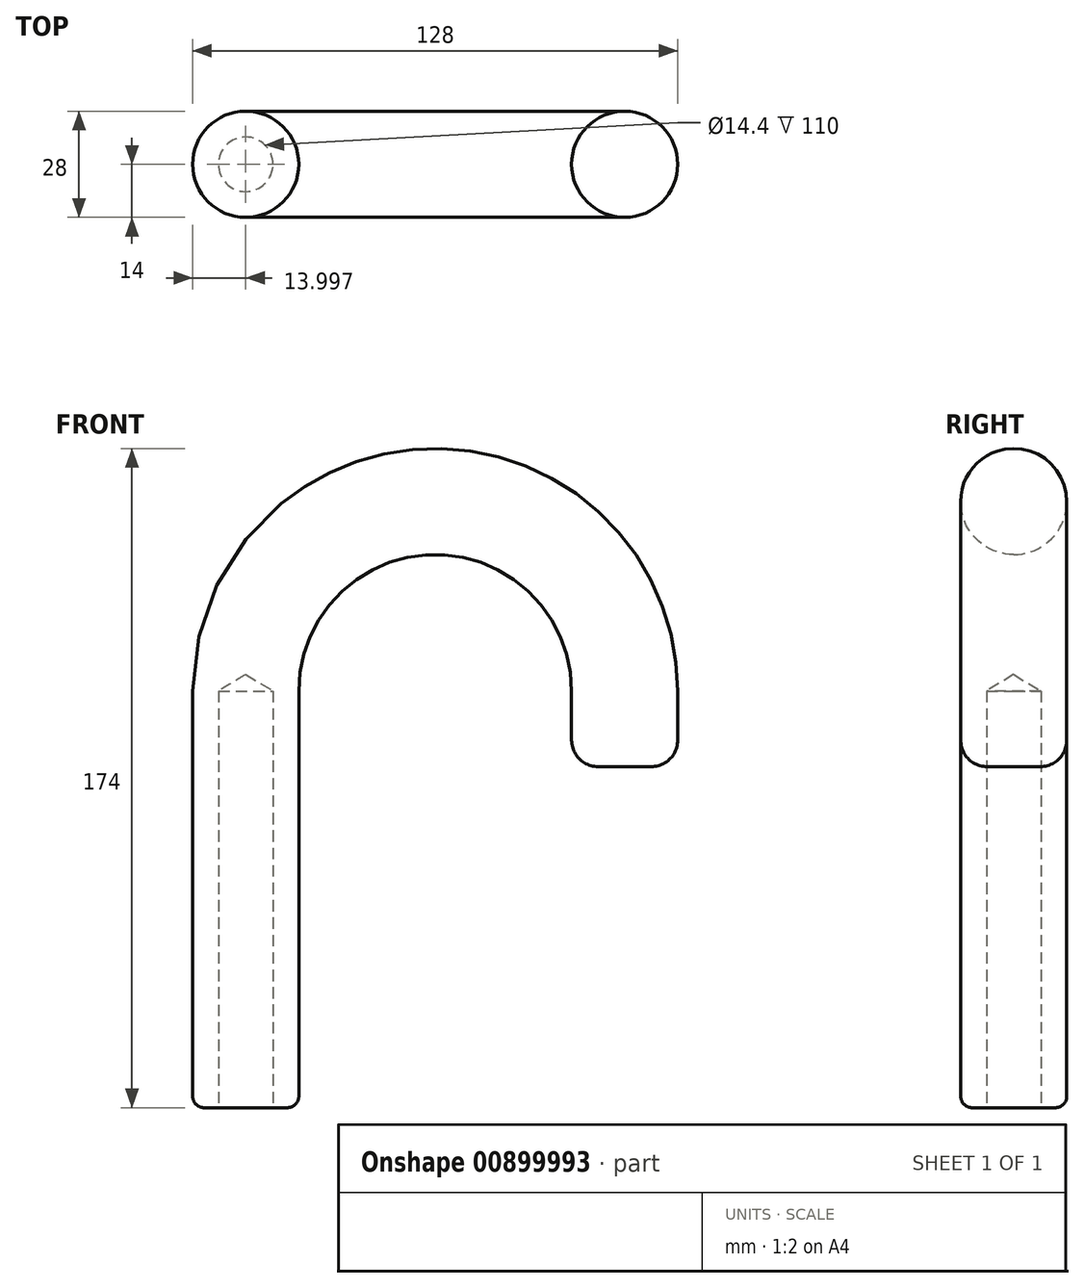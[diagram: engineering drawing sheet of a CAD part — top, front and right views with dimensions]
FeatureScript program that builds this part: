
annotation { "Feature Type Name" : "Feature", "Feature Type Description" : "" }
export const myFeature = defineFeature(function(context is Context, id is Id, definition is map)
    precondition{}
    {
        {
            var Q0;
            Q0=qCreatedBy(makeId("Front.planeOp"),FACE);
            var sketch = newSketch(context, id + "F0", { "sketchPlane" : qUnion([Q0])});
            skLineSegment(sketch, "E0", {"start": v(-34.28, -65.47) * mm, "end": v(-34.28, 44.53) * mm});
            skPoint(sketch, "E1", {"position": v(65.72, 44.53) * mm});
            skLineSegment(sketch, "E2", {"start": v(-34.28, 44.53) * mm, "end": v(65.72, 44.53) * mm});
            skArc(sketch, "E3", {"start": v(65.72, 44.53) * mm, "mid": v(15.72, 94.53) * mm, "end": v(-34.28, 44.53) * mm});
            skLineSegment(sketch, "E4", {"start": v(65.72, 44.53) * mm, "end": v(65.72, 24.53) * mm});
            skSolve(sketch);
        }
        {
            var Q0;
            Q0=sQuery(id+"F0.wireOp",VERTEX,"E0.end");
            var Q1;
            Q1=qCreatedBy(makeId("Top.planeOp"),FACE);
            cPlane(context, id + "F1", {"entities" : qUnion([Q0, Q1]), "cplaneType" : CPlaneType.PLANE_POINT, "offset" : 25 * mm, "width" : 150 * mm, "height" : 150 * mm});
        }
        {
            var Q0;
            Q0=qCreatedBy(id+"F1.planeOp",FACE);
            var sketch = newSketch(context, id + "F2", { "sketchPlane" : qUnion([Q0])});
            skCircle(sketch, "E5", {"center": v(-34.28, 0) * mm, "radius": 14 * mm});
            skSolve(sketch);
        }
        {
            var Q0;
            Q0=makeQuery(id+"F2.imprint","IMPRINT",FACE,{"disambiguationData":[TD([[makeQuery(id+"F2.imprint","IMPRINT",EDGE,{"derivedFrom":sQuery(id+"F2.wireOp",EDGE,"E5")}),1.0]])]});
            extrude(context, id + "F3", {"entities" : qUnion([Q0]), "oppositeDirection" : true, "depth" : 110 * mm, "offsetDistance" : 25 * mm});
        }
        {
            var Q0;
            Q0=makeQuery(id+"F2.imprint","IMPRINT",FACE,{"disambiguationData":[TD([[makeQuery(id+"F2.imprint","IMPRINT",EDGE,{"derivedFrom":sQuery(id+"F2.wireOp",EDGE,"E5")}),1.0]])]});
            var Q1;
            Q1=sQuery(id+"F0.wireOp",EDGE,"E3");
            var Q2;
            Q2=sQuery(id+"F0.wireOp",EDGE,"E4");
            sweep(context, id + "F4", {"operationType" : NewBodyOperationType.ADD, "profiles" : qUnion([Q0]), "path" : qUnion([Q1, Q2])});
        }
        {
            var Q0;
            Q0=makeQuery(id+"F4.opSweep","CAP_FACE",FACE,{"disambiguationData":[OSD([sQuery(id+"F0.wireOp",VERTEX,"E4.end"),sQuery(id+"F2.wireOp",EDGE,"E5")])],"isStart":false});
            fillet(context, id + "F5", {"entities" : qUnion([Q0]), "radius" : 7 * mm, "tangentPropagation" : true, "allowEdgeOverflow" : false});
        }
        {
            var Q0;
            Q0=makeQuery(id+"F3.opExtrude","CAP_FACE",FACE,{"disambiguationData":[OSD([sQuery(id+"F2.wireOp",EDGE,"E5")])],"isStart":false});
            var sketch = newSketch(context, id + "F6", { "sketchPlane" : qUnion([Q0])});
            skPoint(sketch, "E6", {"position": v(-34.28, 0) * mm});
            skSolve(sketch);
        }
        {
            var Q0;
            Q0=sQuery(id+"F6.wireOp",VERTEX,"E6");
            var Q1;
            Q1=makeQuery(id+"F3.opExtrude","SWEPT_BODY",BODY,{"disambiguationData":[OSD([sQuery(id+"F2.wireOp",EDGE,"E5")])]});
            hole(context, id + "F7", {"style" : HoleStyle.SIMPLE, "endStyle" : HoleEndStyle.BLIND, "holeDiameter" : 14.4 * mm, "majorDiameter" : 5 * mm, "holeDepth" : 110 * mm, "isTappedThrough" : true, "tappedDepth" : 12 * mm, "tapClearance" : 3, "locations" : qUnion([Q0]), "scope" : qUnion([Q1])});
        }
        {
            var Q0;
            Q0=makeQuery(id+"F3.opExtrude","CAP_EDGE",EDGE,{"disambiguationData":[OSD([sQuery(id+"F2.wireOp",EDGE,"E5")])],"isStart":false});
            fillet(context, id + "F8", {"entities" : qUnion([Q0]), "radius" : 3 * mm, "tangentPropagation" : true, "allowEdgeOverflow" : false});
        }
    });
